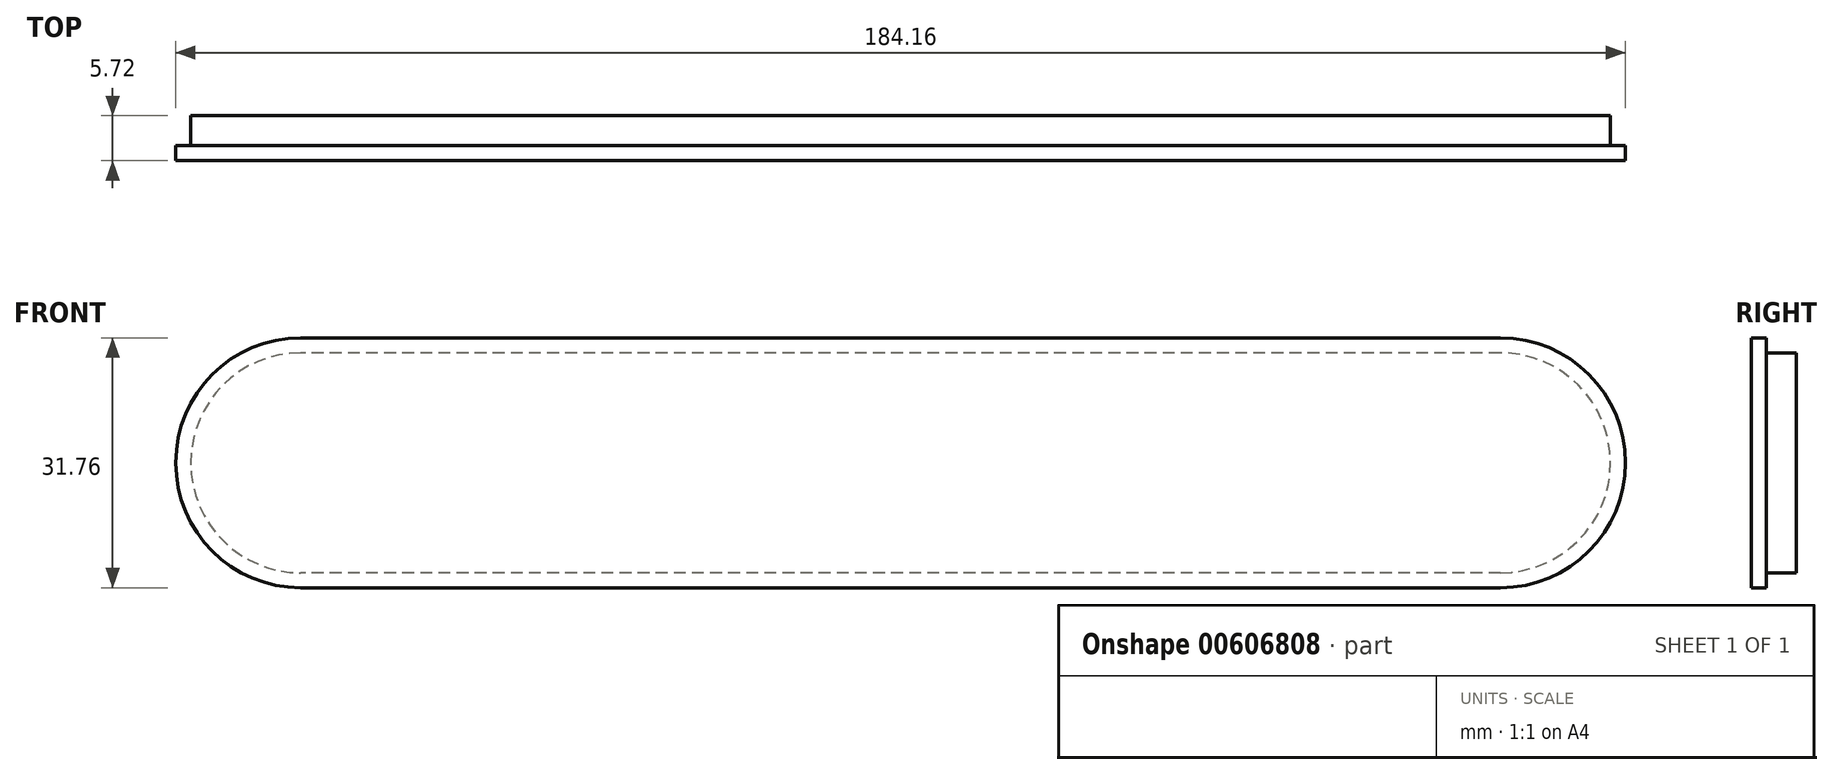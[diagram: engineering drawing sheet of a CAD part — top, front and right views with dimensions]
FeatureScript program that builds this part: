
annotation { "Feature Type Name" : "Feature", "Feature Type Description" : "" }
export const myFeature = defineFeature(function(context is Context, id is Id, definition is map)
    precondition{}
    {
        {
            var Q0;
            Q0=qCreatedBy(makeId("Front.planeOp"),FACE);
            var sketch = newSketch(context, id + "F0", { "sketchPlane" : qUnion([Q0])});
            skLineSegment(sketch, "E0", {"start": v(-76.2, 0) * mm, "end": v(76.2, 0) * mm});
            skLineSegment(sketch, "E1.bottom", {"start": v(76.2, -15.87) * mm, "end": v(-76.2, -15.88) * mm});
            skLineSegment(sketch, "E1.top", {"start": v(76.2, 15.88) * mm, "end": v(-76.2, 15.87) * mm});
            skLineSegment(sketch, "E1.left", {"start": v(76.2, -15.87) * mm, "end": v(76.2, 15.88) * mm});
            skLineSegment(sketch, "E1.right", {"start": v(-76.2, -15.88) * mm, "end": v(-76.2, 15.87) * mm});
            skPoint(sketch, "E1.middle", {"position": v(0, 0) * mm});
            skCircle(sketch, "E2", {"center": v(-76.2, 0) * mm, "radius": 15.88 * mm});
            skCircle(sketch, "E3", {"center": v(76.2, 0) * mm, "radius": 15.88 * mm});
            skSolve(sketch);
        }
        {
            var Q0;
            Q0=qCreatedBy(makeId("Front.planeOp"),FACE);
            var sketch = newSketch(context, id + "F1", { "sketchPlane" : qUnion([Q0])});
            skLineSegment(sketch, "E4.bottom", {"start": v(76.2, 13.97) * mm, "end": v(-76.2, 13.97) * mm});
            skLineSegment(sketch, "E4.top", {"start": v(76.2, -13.97) * mm, "end": v(-76.2, -13.97) * mm});
            skLineSegment(sketch, "E4.left", {"start": v(76.2, 13.97) * mm, "end": v(76.2, -13.97) * mm});
            skLineSegment(sketch, "E4.right", {"start": v(-76.2, 13.97) * mm, "end": v(-76.2, -13.97) * mm});
            skPoint(sketch, "E4.middle", {"position": v(0, 0) * mm});
            skCircle(sketch, "E5", {"center": v(-76.2, 0) * mm, "radius": 13.97 * mm});
            skCircle(sketch, "E6", {"center": v(76.2, 0) * mm, "radius": 13.97 * mm});
            skSolve(sketch);
        }
        {
            var Q0;
            Q0 = qSketchRegion(id + "F0", true);
            extrude(context, id + "F2", {"entities" : qUnion([Q0]), "depth" : 1.9 * mm, "offsetDistance" : 25.4 * mm});
        }
        {
            var Q0;
            Q0 = qSketchRegion(id + "F1", true);
            extrude(context, id + "F3", {"entities" : qUnion([Q0]), "operationType" : NewBodyOperationType.ADD, "oppositeDirection" : true, "depth" : 3.8 * mm, "offsetDistance" : 25.4 * mm});
        }
    });
